# Revit family: Mixer-Bath Shower-Dorf Industrie with Diverter1
name_source: partatom
category: Plumbing Fixtures
revit_build: Autodesk Revit 2014 (Build: 20140709_2115(x64)
units: mm (PartAtom-declared; Revit-internal decimal feet)

## types (3) — shared parameters
Assembly Code = C1030210
CW Connection = Yes
CWFU = 3
Connector Radius = 10 mm  [stored 0.0328084 ft]
Default Elevation = 1000 mm
HW Connection = Yes
HWFU = 3
Height_ANZRS = 137 mm
Length_ANZRS = 70 mm  [stored 0.229659 ft]
Manufacturer = GWA Bathrooms & Kitchens
Material_ANZRS = Metal-Chrome-Caroma
ModifiedIssue_ANZRS = 20160908 $
URL = http://specify.caroma.com.au
Vent Connection = No
Waste Connection = No
Width_ANZRS = 51 mm
zero-valued in all types: Cost

## per-type parameters (varying)
| type | Handle | Model | Type Comments |
| Chrome / Red | Metal-Powdercoat-Red-Caroma | 6119.04 | Dorf Industrie Bath/Shower Mixer with Diverter - Red |
| Chrome / Black | Metal-Powdercoat-Black-Caroma | 6120.04 | Dorf Industrie Bath/Shower Mixer with Diverter - Black |
| Chrome / White | Metal-Powdercoat-White-Caroma | 6121.04 | Dorf Industrie Bath/Shower Mixer with Diverter - White |

note: [stored X ft] marks values corroborated as IEEE doubles in the binary element streams (Revit-internal decimal feet)

## geometry (parser evidence)
native form markers: Blend x10, Sweep x1
no freeform markers — native parametric forms only
